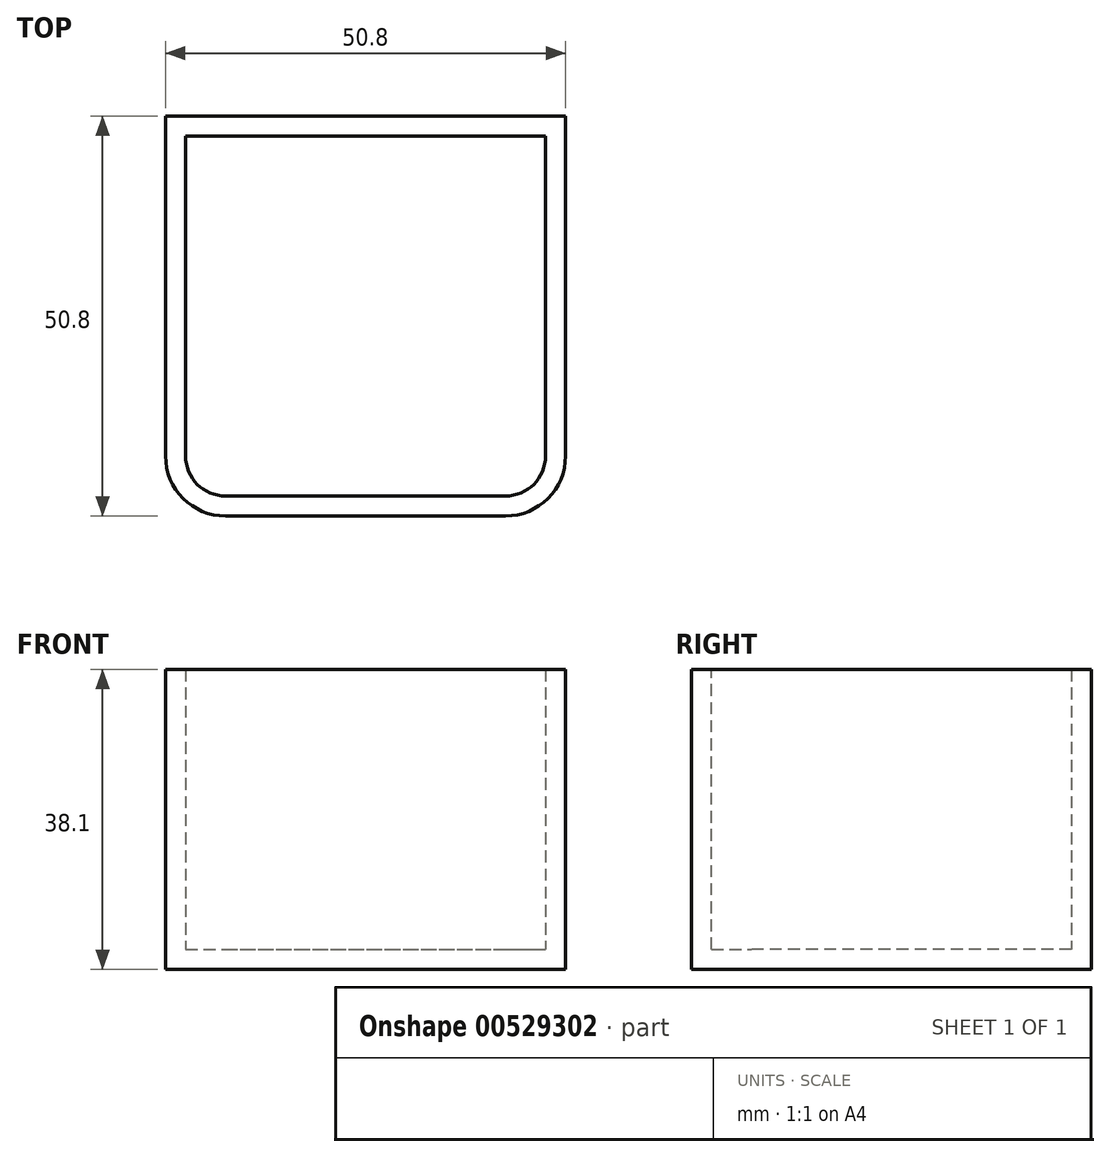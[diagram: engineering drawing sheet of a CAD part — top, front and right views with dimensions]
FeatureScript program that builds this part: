
annotation { "Feature Type Name" : "Feature", "Feature Type Description" : "" }
export const myFeature = defineFeature(function(context is Context, id is Id, definition is map)
    precondition{}
    {
        {
            var Q0;
            Q0=qCreatedBy(makeId("Top.planeOp"),FACE);
            var sketch = newSketch(context, id + "F0", { "sketchPlane" : qUnion([Q0])});
            skLineSegment(sketch, "E0.bottom", {"start": v(0, 0) * mm, "end": v(50.8, 0) * mm});
            skLineSegment(sketch, "E0.top", {"start": v(0, -50.8) * mm, "end": v(50.8, -50.8) * mm});
            skLineSegment(sketch, "E0.left", {"start": v(0, 0) * mm, "end": v(0, -50.8) * mm});
            skLineSegment(sketch, "E0.right", {"start": v(50.8, 0) * mm, "end": v(50.8, -50.8) * mm});
            skSolve(sketch);
        }
        {
            var Q0;
            Q0=makeQuery(id+"F0.imprint","IMPRINT",FACE,{"disambiguationData":[TD([[makeQuery(id+"F0.imprint","IMPRINT",EDGE,{"derivedFrom":sQuery(id+"F0.wireOp",EDGE,"E0.bottom")}),-1.0]])]});
            extrude(context, id + "F1", {"entities" : qUnion([Q0]), "depth" : 38.1 * mm, "offsetDistance" : 25.4 * mm});
        }
        {
            var Q0;
            Q0=makeQuery(id+"F1.opExtrude","SWEPT_EDGE",EDGE,{"disambiguationData":[OSD([sQuery(id+"F0.wireOp",EDGE,"E0.top"),sQuery(id+"F0.wireOp",EDGE,"E0.right")])]});
            var Q1;
            Q1=makeQuery(id+"F1.opExtrude","SWEPT_EDGE",EDGE,{"disambiguationData":[OSD([sQuery(id+"F0.wireOp",EDGE,"E0.top"),sQuery(id+"F0.wireOp",EDGE,"E0.left")])]});
            fillet(context, id + "F2", {"entities" : qUnion([Q0, Q1]), "radius" : 7.62 * mm, "tangentPropagation" : true, "allowEdgeOverflow" : false});
        }
        {
            var Q0;
            Q0=makeQuery(id+"F1.opExtrude","CAP_FACE",FACE,{"disambiguationData":[OSD([sQuery(id+"F0.wireOp",EDGE,"E0.bottom"),sQuery(id+"F0.wireOp",EDGE,"E0.top"),sQuery(id+"F0.wireOp",EDGE,"E0.left"),sQuery(id+"F0.wireOp",EDGE,"E0.right")])],"isStart":false});
            shell(context, id + "F3", {"entities" : qUnion([Q0]), "thickness" : 2.54 * mm});
        }
    });
